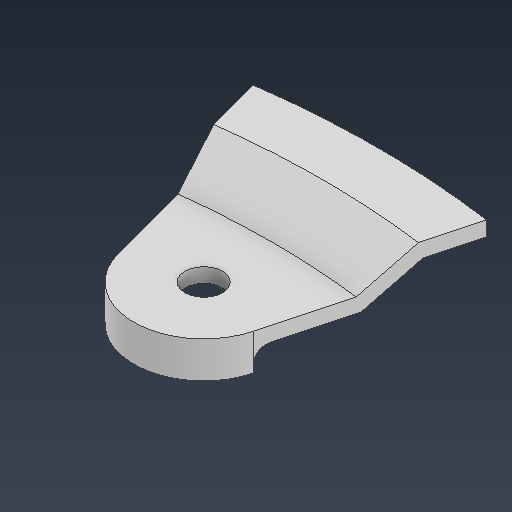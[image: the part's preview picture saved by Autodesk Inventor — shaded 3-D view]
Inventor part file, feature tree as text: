
AUTODESK INVENTOR PART (.ipt)
format: ipt  version: 2025.3 (Build 293356000, 356)  size: 151,552 bytes
history: native  units: mm
features: extrude x3, sketch x2, other x1, fillet x1
ambient origin geometry x8: Origin, YZ Plane, XZ Plane, XY Plane, X Axis, Y Axis, Z Axis, Center Point
bodies: Body1 (feature_tree)
feature tree (7):
  other  "迴轉1"
  sketch  "草圖6"
  extrude  "擠出5"  Depth=2.0mm
  extrude  "擠出8"  Depth=232.0mm
  extrude  "擠出9"  Depth=92.0mm
  fillet  "圓角5"  Radius=2.0mm
  sketch  "草圖5"
